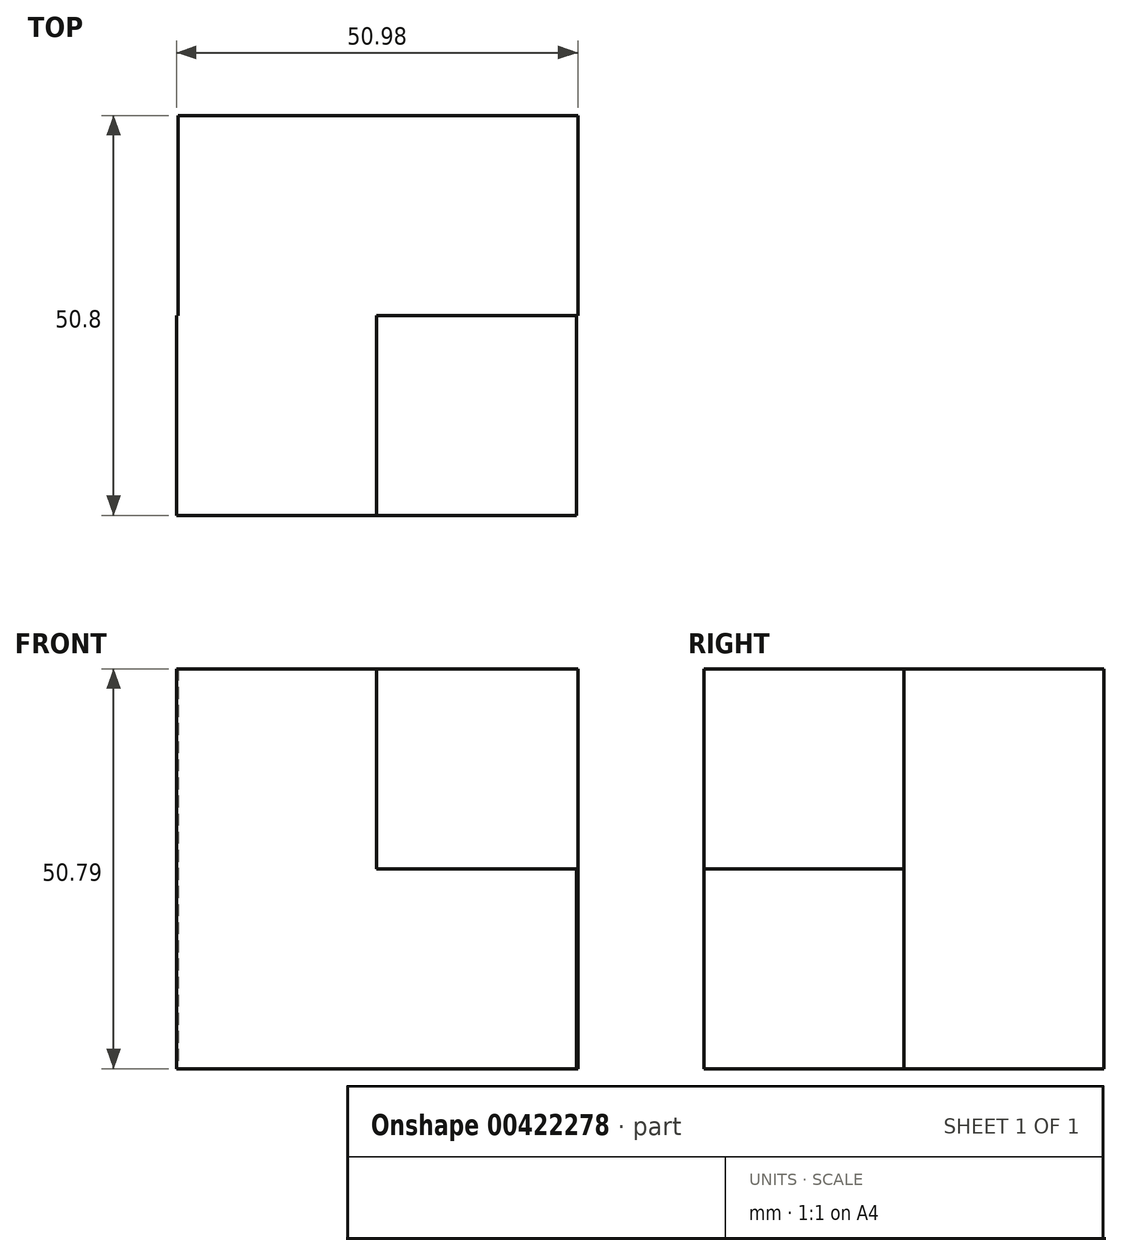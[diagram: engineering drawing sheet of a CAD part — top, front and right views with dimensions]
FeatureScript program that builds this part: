
annotation { "Feature Type Name" : "Feature", "Feature Type Description" : "" }
export const myFeature = defineFeature(function(context is Context, id is Id, definition is map)
    precondition{}
    {
        {
            var Q0;
            Q0=qCreatedBy(makeId("Front.planeOp"),FACE);
            var sketch = newSketch(context, id + "F0", { "sketchPlane" : qUnion([Q0])});
            skLineSegment(sketch, "E0", {"start": v(-40.67, 40.1) * mm, "end": v(-40.67, -10.7) * mm});
            skLineSegment(sketch, "E1", {"start": v(-40.67, -10.7) * mm, "end": v(10.12, -10.7) * mm});
            skLineSegment(sketch, "E2", {"start": v(10.12, -10.7) * mm, "end": v(10.12, 14.7) * mm});
            skLineSegment(sketch, "E3", {"start": v(10.12, 14.7) * mm, "end": v(-15.28, 14.7) * mm});
            skLineSegment(sketch, "E4", {"start": v(-15.28, 14.7) * mm, "end": v(-15.28, 40.1) * mm});
            skLineSegment(sketch, "E5", {"start": v(-15.28, 40.1) * mm, "end": v(-40.67, 40.1) * mm});
            skSolve(sketch);
        }
        {
            var Q0;
            Q0=qCreatedBy(makeId("Front.planeOp"),FACE);
            var sketch = newSketch(context, id + "F1", { "sketchPlane" : qUnion([Q0])});
            skLineSegment(sketch, "E6.bottom", {"start": v(-40.48, 40.1) * mm, "end": v(10.31, 40.1) * mm});
            skLineSegment(sketch, "E6.top", {"start": v(-40.48, -10.7) * mm, "end": v(10.31, -10.7) * mm});
            skLineSegment(sketch, "E6.left", {"start": v(-40.48, 40.1) * mm, "end": v(-40.48, -10.7) * mm});
            skLineSegment(sketch, "E6.right", {"start": v(10.31, 40.1) * mm, "end": v(10.31, -10.7) * mm});
            skSolve(sketch);
        }
        {
            var Q0;
            Q0=makeQuery(id+"F1.imprint","IMPRINT",FACE,{"disambiguationData":[TD([[makeQuery(id+"F1.imprint","IMPRINT",EDGE,{"derivedFrom":sQuery(id+"F1.wireOp",EDGE,"E6.bottom")}),-1.0]])]});
            extrude(context, id + "F2", {"entities" : qUnion([Q0]), "depth" : -25.4 * mm});
        }
        {
            var Q0;
            Q0=makeQuery(id+"F0.imprint","IMPRINT",FACE,{"disambiguationData":[TD([[makeQuery(id+"F0.imprint","IMPRINT",EDGE,{"derivedFrom":sQuery(id+"F0.wireOp",EDGE,"E0")}),1.0]])]});
            extrude(context, id + "F3", {"entities" : qUnion([Q0]), "operationType" : NewBodyOperationType.ADD, "depth" : 25.4 * mm});
        }
    });
